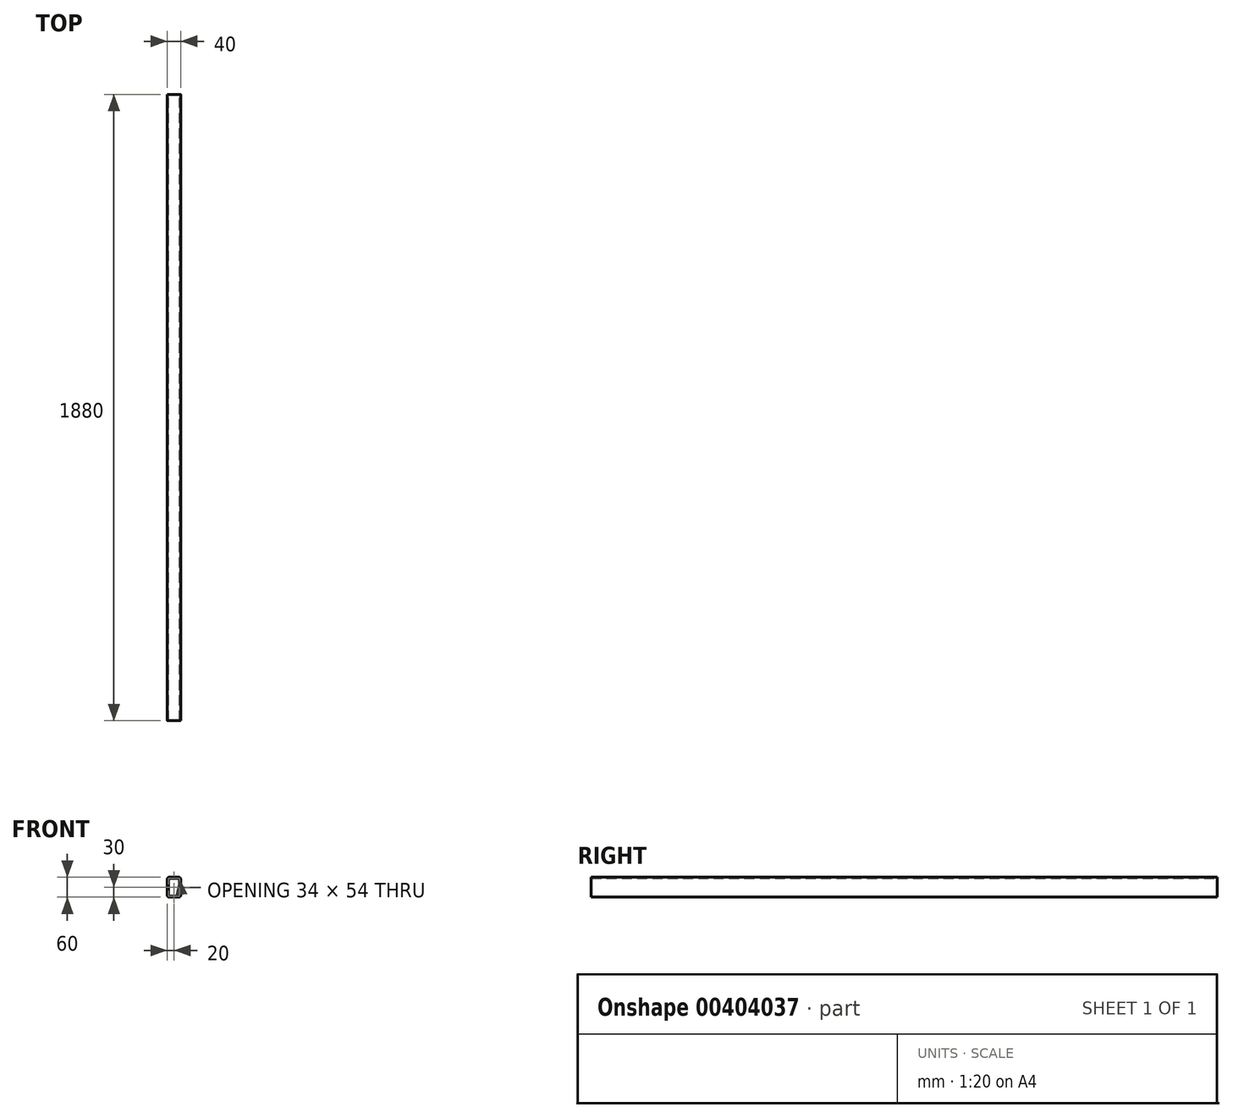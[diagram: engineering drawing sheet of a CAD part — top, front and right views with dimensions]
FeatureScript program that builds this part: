
annotation { "Feature Type Name" : "Feature", "Feature Type Description" : "" }
export const myFeature = defineFeature(function(context is Context, id is Id, definition is map)
    precondition{}
    {
        {
            var Q0;
            Q0=qCreatedBy(makeId("Front.planeOp"),FACE);
            var sketch = newSketch(context, id + "F0", { "sketchPlane" : qUnion([Q0])});
            skLineSegment(sketch, "E0.bottom", {"start": v(-14, 30) * mm, "end": v(14, 30) * mm});
            skLineSegment(sketch, "E0.top", {"start": v(-14, -30) * mm, "end": v(14, -30) * mm});
            skLineSegment(sketch, "E0.left", {"start": v(-20, 24) * mm, "end": v(-20, -24) * mm});
            skLineSegment(sketch, "E0.right", {"start": v(20, 24) * mm, "end": v(20, -24) * mm});
            skPoint(sketch, "E1.visualSharp", {"position": v(-20, 30) * mm});
            skArc(sketch, "E1.filletArc", {"start": v(-14, 30) * mm, "mid": v(-18.24, 28.24) * mm, "end": v(-20, 24) * mm});
            skPoint(sketch, "E2.visualSharp", {"position": v(-20, -30) * mm});
            skArc(sketch, "E2.filletArc", {"start": v(-20, -24) * mm, "mid": v(-18.24, -28.24) * mm, "end": v(-14, -30) * mm});
            skPoint(sketch, "E3.visualSharp", {"position": v(20, -30) * mm});
            skArc(sketch, "E3.filletArc", {"start": v(14, -30) * mm, "mid": v(18.24, -28.24) * mm, "end": v(20, -24) * mm});
            skPoint(sketch, "E4.visualSharp", {"position": v(20, 30) * mm});
            skArc(sketch, "E4.filletArc", {"start": v(20, 24) * mm, "mid": v(18.24, 28.24) * mm, "end": v(14, 30) * mm});
            skLineSegment(sketch, "E5.0", {"start": v(-17, 24) * mm, "end": v(-17, -24) * mm});
            skLineSegment(sketch, "E6.0", {"start": v(-14, 27) * mm, "end": v(14, 27) * mm});
            skArc(sketch, "E6.1", {"start": v(17, 24) * mm, "mid": v(16.12, 26.12) * mm, "end": v(14, 27) * mm});
            skLineSegment(sketch, "E6.2", {"start": v(17, 24) * mm, "end": v(17, -24) * mm});
            skArc(sketch, "E6.4", {"start": v(-17, -24) * mm, "mid": v(-16.12, -26.12) * mm, "end": v(-14, -27) * mm});
            skLineSegment(sketch, "E6.5", {"start": v(-14, -27) * mm, "end": v(14, -27) * mm});
            skArc(sketch, "E6.6", {"start": v(14, -27) * mm, "mid": v(16.12, -26.12) * mm, "end": v(17, -24) * mm});
            skArc(sketch, "E7.0", {"start": v(-14, 27) * mm, "mid": v(-16.12, 26.12) * mm, "end": v(-17, 24) * mm});
            skSolve(sketch);
        }
        {
            var Q0;
            Q0=makeQuery(id+"F0.imprint","IMPRINT",FACE,{"disambiguationData":[TD([[makeQuery(id+"F0.imprint","IMPRINT",EDGE,{"derivedFrom":sQuery(id+"F0.wireOp",EDGE,"E0.bottom")}),-1.0]])]});
            extrude(context, id + "F1", {"entities" : qUnion([Q0]), "depth" : 1880 * mm});
        }
    });
